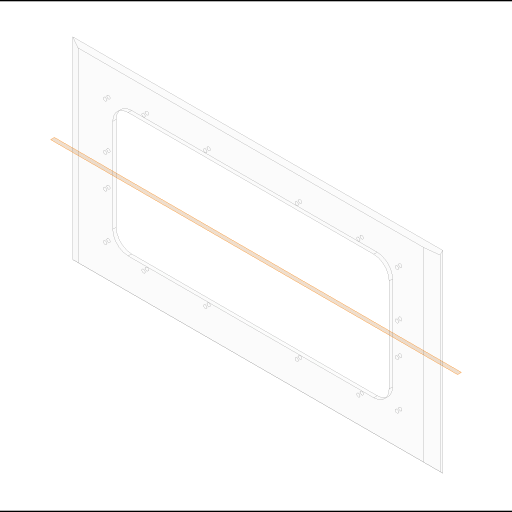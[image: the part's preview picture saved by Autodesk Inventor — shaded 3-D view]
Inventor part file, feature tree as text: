
AUTODESK INVENTOR PART (.ipt)
format: ipt  version: 2023 (Build 270158000, 158)  size: 217,088 bytes
history: native  units: in
note: dims shown in document units (in); Inventor stores cm internally (conversion verified against a paired STEP export)
features: extrude x6, sketch x6, projected_geometry x3, other x1
ambient origin geometry x8: Origin, YZ Plane, XZ Plane, XY Plane, X Axis, Y Axis, Z Axis, Center Point
bodies: Solid1 (feature_tree)
feature tree (16):
  extrude  "Extrusion1"  Depth=12.515in
  extrude  "Extrusion2"  Depth=0.227in
  extrude  "Extrusion3"  TaperAngle=0.0deg  [1 undecoded]
  other  "Center Plane"
  extrude  "Extrusion4"  TaperAngle=135.0deg  [1 undecoded]
  extrude  "Extrusion5"  Depth=6.2575in
  extrude  "Extrusion6"  Depth=1.0in
  sketch  "Sketch1"  dims[d0=24.0in d1=12.515in]
  sketch  "Sketch2"  dims[d2=0.227in d3=0.0in d4=0.1494in]
  projected_geometry  "Projected Loop1"
  sketch  "Sketch3"  dims[d5=90.0deg d6=0.0in d7=0.0in]
  projected_geometry  "Projected Loop2"
  sketch  "Sketch4"  dims[d8=135.0deg d9=135.0deg]
  projected_geometry  "Projected Loop3"
  sketch  "Sketch5"  dims[d10=0.0in d11=0.0in d12=6.2575in]
  sketch  "Sketch6"  dims[d13=1.0in d14=0.0205in d15=6.083in d16=0.0in d18=2.0in d19=2.0in d20=2.25in d21=2.25in d22=1.0in d23=0.0in d24=0.0in d25=0.217in d26=0.217in d27=0.2165in d28=0.217in d29=0.5in d30=1.0in d31=3.0in d32=2.061in d33=3.0in d34=0.5in d35=0.5in d36=0.5in d37=0.7874in d39=18.931in d40=0.3937in d42=1.0in d44=0.217in d45=0.217in d46=0.217in d48=2.5in d49=0.35in d50=0.35in d51=0.35in d53=4.0in d54=5.931in d55=0.217in d56=4.0in d57=0.35in d58=0.3937in d60=1.0in d61=0.7874in d63=8.761in d65=0.0in d66=0.0in]
note: 2 required parameter values undecoded (feature->parameter linkage not recoverable at this tier; creation-order binding heuristic only, values carry confidence <= 0.55)
